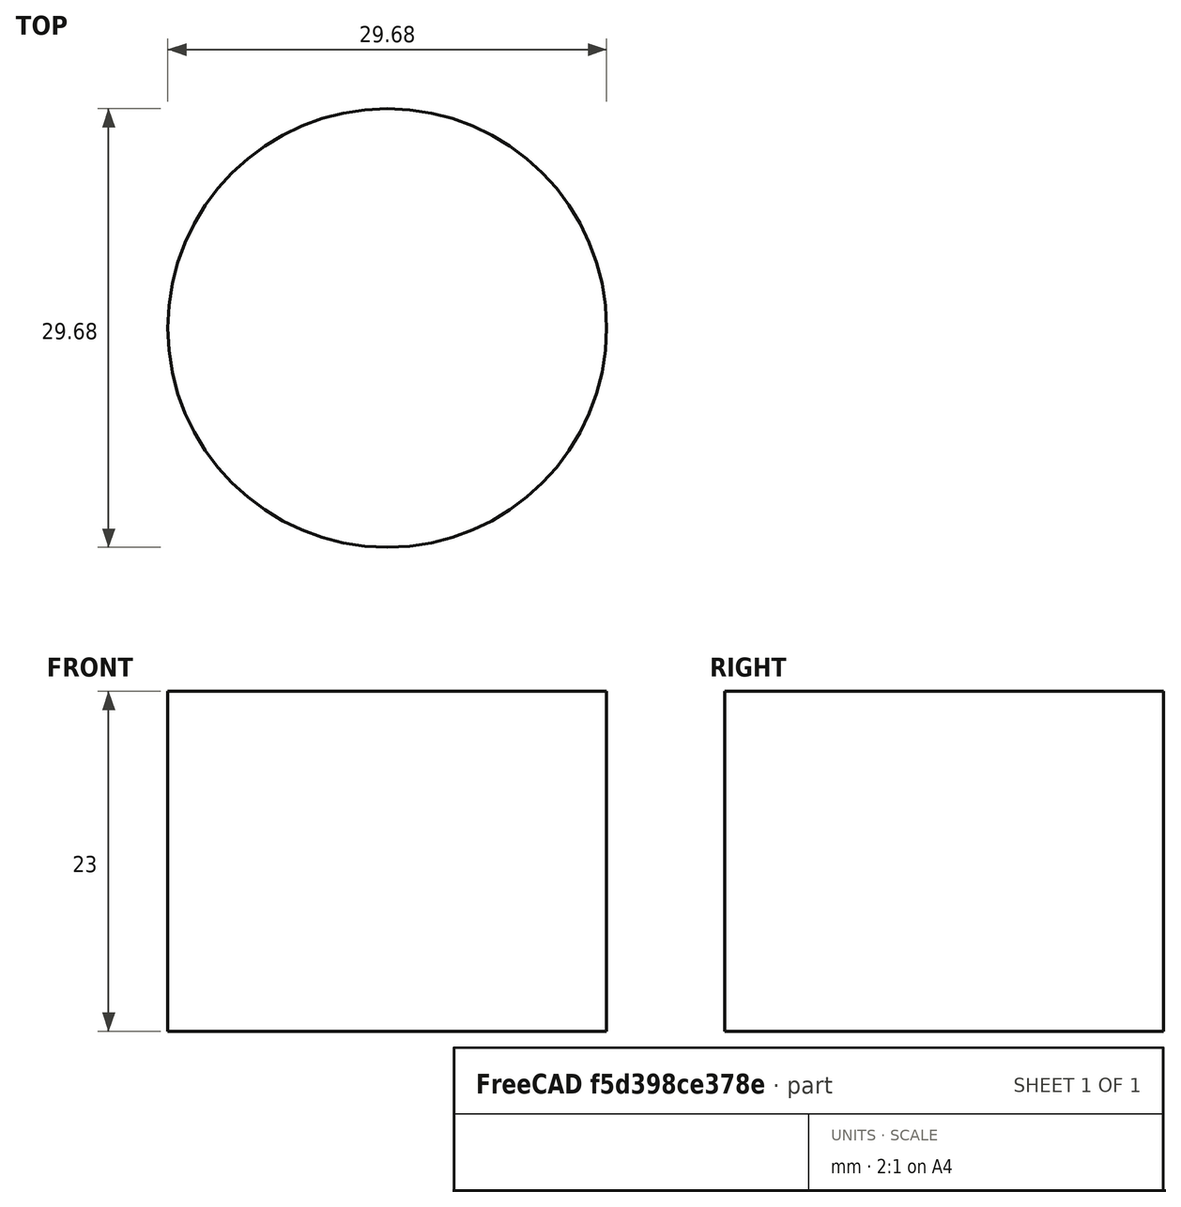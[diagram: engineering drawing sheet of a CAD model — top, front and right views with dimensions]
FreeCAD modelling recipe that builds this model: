
FCSTD DOCUMENT  (FreeCAD 0.17R13519 (Git))
Label: SFP-Puller2
License: All rights reserved
LicenseURL: http://en.wikipedia.org/wiki/All_rights_reserved
objects: TechDraw::DrawViewDimension×18, Sketcher::SketchObject×3, PartDesign::Pad×3, PartDesign::Fillet×3, Drawing::FeatureViewPart×3, TechDraw::DrawViewPart×3, Path::FeaturePython×3, Part::FeaturePython×2, PartDesign::Point×1, PartDesign::Line×1, PartDesign::SubtractiveCylinder×1, PartDesign::Pocket×1, PartDesign::Body×1, Drawing::FeaturePage×1, TechDraw::DrawSVGTemplate×1, TechDraw::DrawViewAnnotation×1, TechDraw::DrawPage×1, App::FeaturePython×1, Path::FeatureCompoundPython×1
note: 22 computed .brp shape members not serialized (recipe doc carries the construction recipe); baked Part::Feature solids carry a one-line shape summary decoded from their .brp

FEATURE [Sketcher::SketchObject] Sketch
  MapMode = 5
  Support = -> [XY_Plane]
  sketch-geometry (18):
    g0: LineSegment StartX=-1 StartY=5.95091 StartZ=0 EndX=-1 EndY=-5.54909 EndZ=0
    g1: LineSegment StartX=-1 StartY=-5.54909 StartZ=0 EndX=-8 EndY=-5.54909 EndZ=0
    g2: LineSegment StartX=-8 StartY=-5.54909 StartZ=0 EndX=-8 EndY=-9.54909 EndZ=0
    g3: LineSegment StartX=-8 StartY=-9.54909 StartZ=0 EndX=-4.78208 EndY=-12.304 EndZ=0
    g4: LineSegment StartX=-4.78208 StartY=-12.304 StartZ=0 EndX=-6.93768 EndY=-14.8219 EndZ=0
    g5: LineSegment StartX=-6.93768 StartY=-14.8219 StartZ=0 EndX=-2 EndY=-19.0491 EndZ=0
    g6: LineSegment StartX=-2 StartY=-19.0491 StartZ=0 EndX=0 EndY=-19.0491 EndZ=0
    g7: LineSegment StartX=-1 StartY=5.95091 StartZ=0 EndX=0 EndY=5.95091 EndZ=0
    g8: GeomPoint X=0 Y=-19.0491 Z=0
    g9: LineSegment StartX=0 StartY=-19.0491 StartZ=0 EndX=1 EndY=-19.0491 EndZ=0
    g10: LineSegment StartX=1 StartY=-19.0491 StartZ=0 EndX=1 EndY=-7.54909 EndZ=0
    g11: LineSegment StartX=1 StartY=-7.54909 StartZ=0 EndX=8 EndY=-7.54909 EndZ=0
    g12: LineSegment StartX=8 StartY=-7.54909 StartZ=0 EndX=8 EndY=-3.54909 EndZ=0
    g13: LineSegment StartX=8 StartY=-3.54909 StartZ=0 EndX=4.81331 EndY=-0.531755 EndZ=0
    g14: LineSegment StartX=4.81331 StartY=-0.531755 StartZ=0 EndX=6.7199 EndY=1.48185 EndZ=0
    g15: LineSegment StartX=6.7199 StartY=1.48185 StartZ=0 EndX=2 EndY=5.95091 EndZ=0
    g16: LineSegment StartX=0 StartY=5.95091 StartZ=0 EndX=2 EndY=5.95091 EndZ=0
    g17: GeomPoint X=0 Y=-6.54909 Z=0
  constraints (47):
    c: Vertical(g0)
    c: Coincident(g0,g1)
    c: Coincident(g1,g2)
    c: Vertical(g2)
    c: Coincident(g2,g3)
    c: Coincident(g3,g4)
    c: Coincident(g4,g5)
    c: Coincident(g6,g5)
    c: Horizontal(g6)
    c: Perpendicular(g1,g0)
    c: Perpendicular(g3,g4)
    c: Perpendicular(g4,g5)
    c: Coincident(g7,g0)
    c: PointOnObject(g7,g-2)
    c: Horizontal(g7)
    c: DistanceX(g7,g7) = 1
    c: DistanceX(g1,g1) = 7
    c: DistanceX(g6,g6) = 2
    c: PointOnObject(g8,g-2)
    c: Coincident(g8,g6)
    c: DistanceY(g2,g2) = 4
    c: Horizontal(g9)
    c: DistanceX(g9,g9) = 1
    c: Coincident(g9,g6)
    c: Vertical(g10)
    c: Coincident(g10,g9)
    c: Coincident(g11,g10)
    c: DistanceX(g11,g11) = 7
    c: Vertical(g12)
    c: DistanceY(g12,g12) = -4
    c: Coincident(g12,g11)
    c: Perpendicular(g11,g10)
    c: Coincident(g13,g12)
    c: Coincident(g14,g13)
    c: Perpendicular(g13,g14)
    c: Coincident(g15,g14)
    c: Perpendicular(g14,g15)
    c: Horizontal(g16)
    c: DistanceX(g16,g16) = 2
    c: Coincident(g16,g7)
    c: Coincident(g15,g16)
    c: DistanceY(g6,g7) = 25
    c: DistanceY(g10,g10) = 11.5
    c: DistanceY(g0,g0) = 11.5
    c: Symmetric(g0,g10,g17)  'RootPoint'
    c: Distance(g5) = 6.5
    c: Distance(g15) = 6.5
FEATURE [PartDesign::Pad] Pad
  Length = 3
  Length2 = 100
  Profile = -> Sketch
  Type = 0
FEATURE [PartDesign::Point] DatumPoint
  AttacherType = Attacher::AttachEnginePoint
  MapMode = 37
  Placement = pos=(-0.0215319,-6.59893,0) rot=(0,0,1;0rad)
  Support = -> [Pad]
FEATURE [PartDesign::Line] DatumLine
  AttacherType = Attacher::AttachEngineLine
  MapMode = 42
  Placement = pos=(-0.0215319,-6.59893,0) rot=(0,0,1;0rad)
  Support = -> [Pad]
FEATURE [Sketcher::SketchObject] Sketch001
  AttachmentOffset = pos=(0.26,-7.14,3) rot=(0,0,1;0rad)
  MapMode = 5
  Placement = pos=(0.26,-7.14,3) rot=(0,0,1;0rad)
  Support = -> [XY_Plane]
  sketch-geometry (1):
    g0: Circle CenterX=0 CenterY=0 CenterZ=0 NormalX=0 NormalY=0 NormalZ=1 AngleXU=0 Radius=5
  constraints (2):
    c: Radius(g0) = 5
    c: Coincident(g0,g-1)
FEATURE [PartDesign::Pad] Pad001
  BaseFeature = -> Pad
  Length = 20
  Length2 = 100
  Profile = -> Sketch001
  Type = 0
FEATURE [PartDesign::SubtractiveCylinder] Cylinder
  Angle = 360
  AttacherType = Attacher::AttachEngine3D
  AttachmentOffset = pos=(0.26,-7.14,0) rot=(0,0,1;0rad)
  BaseFeature = -> Pad001
  Height = 10
  MapMode = 5
  Placement = pos=(0.26,-7.14,23) rot=(0,0,1;0rad)
  Radius = 2.5
  Support = -> [Pad001]
FEATURE [PartDesign::Pocket] Pocket
  BaseFeature = -> Cylinder
  Length = 20
  Length2 = 100
  Placement = pos=(0.26,-7.14,23) rot=(0,0,1;0rad)
  Profile = -> Cylinder [Face24]
  Type = 0
FEATURE [Sketcher::SketchObject] Sketch002
  MapMode = 2
  Support = -> [Sketch]
  sketch-geometry (2):
    g0: GeomPoint X=0.26 Y=-7.14 Z=0
    g1: Circle CenterX=0.26 CenterY=-7.14 CenterZ=0 NormalX=0 NormalY=0 NormalZ=1 AngleXU=0 Radius=5
  constraints (4):
    c: DistanceX(g0) = 0.26
    c: DistanceY(g0) = -7.14
    c: Coincident(g1,g0)
    c: Radius(g1) = 5
FEATURE [PartDesign::Pad] Pad002
  BaseFeature = -> Pocket
  Length = 3
  Length2 = 100
  Placement = pos=(0.26,-7.14,23) rot=(0,0,1;0rad)
  Profile = -> Sketch002
  Type = 0
FEATURE [PartDesign::Fillet] Fillet
  Base = -> Pad002 [Edge8,Edge1,Edge63,Edge65,Edge31,Edge43]
  BaseFeature = -> Pad002
  Placement = pos=(0.26,-7.14,23) rot=(0,0,1;0rad)
  Radius = 0.95
FEATURE [PartDesign::Fillet] Fillet001
  Base = -> Fillet [Edge21,Edge18,Edge68,Edge70,Edge26,Edge71]
  BaseFeature = -> Fillet
  Placement = pos=(0.26,-7.14,23) rot=(0,0,1;0rad)
  Radius = 0.5
FEATURE [PartDesign::Fillet] Fillet002
  Base = -> Fillet001 [Edge58,Edge69]
  BaseFeature = -> Fillet001
  Placement = pos=(0.26,-7.14,23) rot=(0,0,1;0rad)
  Radius = 1
FEATURE [PartDesign::Body] Body
  Group = -> [Sketch,Pad,DatumPoint,DatumLine,Sketch001,Pad001,Cylinder,Pocket,Sketch002,Pad002,Fillet,Fillet001,Fillet002]
  Origin = -> Origin
  Tip = -> Fillet002
FEATURE [Drawing::FeatureViewPart] View
  Direction = (0,0,1)
  HiddenWidth = 0.15
  LineWidth = 0.35
  Rotation = 0
  Scale = 4
  ShowHiddenLines = true
  ShowSmoothLines = true
  Source = -> Body
  Tolerance = 0.05
  ViewResult = <blob: 11207 chars omitted>
  Visible = true
  X = 55
  Y = 45
FEATURE [Drawing::FeatureViewPart] View001
  Direction = (0,1,0)
  HiddenWidth = 0.15
  LineWidth = 0.35
  Rotation = 0
  Scale = 4
  ShowHiddenLines = true
  ShowSmoothLines = false
  Source = -> Body
  Tolerance = 0.05
  ViewResult = <blob: 10966 chars omitted>
  Visible = true
  X = 150
  Y = 55
FEATURE [Drawing::FeatureViewPart] View002
  Direction = (1,1,1)
  HiddenWidth = 0.15
  LineWidth = 0.35
  Rotation = 0
  Scale = 4
  ShowHiddenLines = true
  ShowSmoothLines = true
  Source = -> Body
  Tolerance = 0.05
  ViewResult = <blob: 16132 chars omitted>
  Visible = true
  X = 100
  Y = 110
FEATURE [Drawing::FeaturePage] Page
  EditableTexts = J Miller | 10-JUL-2018 | 4:1 | NA | SFP Pusher Adapter | Aluminium or engineering plastic | FCAD1 | 1
  Group = -> [View,View001,View002]
  Template = /Applications/FreeCAD.app/Contents/data/Mod/Drawing/Templates/A4_Landscape.svg
FEATURE [TechDraw::DrawSVGTemplate] Template
  EditableTexts = Designed_by_Name=J Miller; Drawing_number=FCAD-002; FC-Date=7-JUL-2018; FC-SC=4:1; FC-SH=1; FC-Title=Medrad-Puller; Subtitle=Aluminium or hard engineering plastic; Weight=NA
  Height = 210
  Orientation = 1
  Width = 297
FEATURE [TechDraw::DrawViewPart] View003  label="Top"
  CoarseView = true
  Direction = (0,0,1)
  Focus = 100
  HardHidden = true
  IsoCount = 0
  IsoHidden = true
  IsoVisible = true
  LockPosition = false
  Perspective = false
  Rotation = 0
  Scale = 4
  ScaleType = 0
  SeamHidden = true
  SeamVisible = true
  SmoothHidden = true
  SmoothVisible = true
  Source = -> [Body]
  X = 141.747
  Y = 133.6
FEATURE [TechDraw::DrawViewPart] View004  label="Side"
  CoarseView = true
  Direction = (1,0,0)
  Focus = 100
  HardHidden = true
  IsoCount = 0
  IsoHidden = false
  IsoVisible = true
  LockPosition = false
  Perspective = false
  Rotation = 0
  Scale = 4
  ScaleType = 0
  SeamHidden = true
  SeamVisible = true
  SmoothHidden = true
  SmoothVisible = true
  Source = -> [Body]
  X = 229.007
  Y = 104.62
FEATURE [TechDraw::DrawViewPart] View005  label="Third Angle"
  CoarseView = true
  Direction = (1,0,1)
  Focus = 100
  HardHidden = true
  IsoCount = 0
  IsoHidden = true
  IsoVisible = true
  LockPosition = false
  Perspective = false
  Rotation = 0
  Scale = 4
  ScaleType = 0
  SeamHidden = true
  SeamVisible = true
  SmoothHidden = true
  SmoothVisible = true
  Source = -> [Body]
  X = 60
  Y = 60
FEATURE [TechDraw::DrawViewDimension] Dimension
  FormatSpec = %.2f
  LockPosition = false
  MeasureType = 1
  References2D = -> [View004]
  Rotation = 0
  ScaleType = 0
  Type = 2
  X = -50
  Y = 0
FEATURE [TechDraw::DrawViewDimension] Dimension001
  FormatSpec = %.2f
  LockPosition = false
  MeasureType = 1
  References2D = -> [View004]
  Rotation = 0
  ScaleType = 0
  Type = 2
  X = -27.2112
  Y = 1.54609
FEATURE [TechDraw::DrawViewAnnotation] Annotation
  Font = osifont
  LineSpace = 80
  LockPosition = false
  MaxWidth = -1
  Rotation = 0
  ScaleType = 0
  Text = OD ø10 mm | ID M6 Tap (ø5 mm)
  TextSize = 8
  TextStyle = 0
  X = 46.3549
  Y = 180.581
FEATURE [TechDraw::DrawViewDimension] Dimension002
  FormatSpec = %.2f
  LockPosition = false
  MeasureType = 1
  References2D = -> [View003]
  Rotation = 0
  ScaleType = 0
  Type = 1
  X = 12.2377
  Y = -57.8095
FEATURE [TechDraw::DrawViewDimension] Dimension003
  FormatSpec = %.2f
  LockPosition = false
  MeasureType = 1
  References2D = -> [View003]
  Rotation = 0
  ScaleType = 0
  Type = 2
  X = -60.7966
  Y = 1.4057
FEATURE [TechDraw::DrawViewDimension] Dimension004
  FormatSpec = %.2f
  LockPosition = false
  MeasureType = 1
  References2D = -> [View003]
  Rotation = 0
  ScaleType = 0
  Type = 2
  X = -53.9438
  Y = -5.4471
FEATURE [TechDraw::DrawViewDimension] Dimension005
  FormatSpec = %.2f
  LockPosition = false
  MeasureType = 1
  References2D = -> [View003]
  Rotation = 0
  ScaleType = 0
  Type = 2
  X = -49.0239
  Y = -12.1242
FEATURE [TechDraw::DrawViewDimension] Dimension006
  FormatSpec = %.2f
  LockPosition = false
  MeasureType = 1
  References2D = -> [View003]
  Rotation = 0
  ScaleType = 0
  Type = 2
  X = -41.1168
  Y = -14.057
FEATURE [TechDraw::DrawViewDimension] Dimension007
  FormatSpec = %.2f
  LockPosition = false
  MeasureType = 1
  References2D = -> [View003]
  Rotation = 0
  ScaleType = 0
  Type = 0
  X = 11.8617
  Y = 46.1075
FEATURE [TechDraw::DrawViewDimension] Dimension008
  FormatSpec = %.2f
  LockPosition = false
  MeasureType = 1
  References2D = -> [View003]
  Rotation = 0
  ScaleType = 0
  Type = 0
  X = 34.0545
  Y = 28.6976
FEATURE [TechDraw::DrawViewDimension] Dimension009
  FormatSpec = %.2f
  LockPosition = false
  MeasureType = 1
  References2D = -> [View003]
  Rotation = 0
  ScaleType = 0
  Type = 0
  X = -16.4533
  Y = -24.68
FEATURE [TechDraw::DrawViewDimension] Dimension010
  FormatSpec = %.2f
  LockPosition = false
  MeasureType = 1
  References2D = -> [View003]
  Rotation = 0
  ScaleType = 0
  Type = 2
  X = -40.3342
  Y = 17.8052
FEATURE [TechDraw::DrawViewDimension] Dimension011
  FormatSpec = %.2f
  LockPosition = false
  MeasureType = 1
  References2D = -> [View003]
  Rotation = 0
  ScaleType = 0
  Type = 2
  X = -24.1642
  Y = 51.962
FEATURE [TechDraw::DrawViewDimension] Dimension012
  FormatSpec = %.2f
  LockPosition = false
  MeasureType = 1
  References2D = -> [View003]
  Rotation = 0
  ScaleType = 0
  Type = 2
  X = -15.8066
  Y = 40.8792
FEATURE [TechDraw::DrawViewDimension] Dimension013
  FormatSpec = %.2f
  LockPosition = false
  MeasureType = 1
  References2D = -> [View004]
  Rotation = 0
  ScaleType = 0
  Type = 2
  X = 43.1988
  Y = -3.7388
FEATURE [TechDraw::DrawViewDimension] Dimension014
  FormatSpec = %.2f
  LockPosition = false
  MeasureType = 1
  References2D = -> [View003]
  Rotation = 0
  ScaleType = 0
  Type = 6
  X = 8.33551
  Y = 35.5784
FEATURE [TechDraw::DrawViewDimension] Dimension015
  FormatSpec = %.2f
  LockPosition = false
  MeasureType = 1
  References2D = -> [View003]
  Rotation = 0
  ScaleType = 0
  Type = 6
  X = 21.957
  Y = 13.8248
FEATURE [TechDraw::DrawViewDimension] Dimension016
  FormatSpec = %.2f
  LockPosition = false
  MeasureType = 1
  References2D = -> [View003]
  Rotation = 0
  ScaleType = 0
  Type = 1
  X = 24.3966
  Y = -13.8248
FEATURE [TechDraw::DrawViewDimension] Dimension017
  FormatSpec = %.2f
  LockPosition = false
  MeasureType = 1
  References2D = -> [View003]
  Rotation = 0
  ScaleType = 0
  Type = 1
  X = -23.5834
  Y = 33.952
FEATURE [TechDraw::DrawPage] Page001
  KeepUpdated = true
  ProjectionType = 0
  Template = -> Template
  Views = -> [View003,View004,View005,Dimension,Dimension001,Annotation,Dimension002,Dimension003,Dimension004,Dimension005,Dimension006,Dimension007,Dimension008,Dimension009,Dimension010,Dimension011,Dimension012,Dimension013,Dimension014,Dimension015,Dimension016,Dimension017]
FEATURE [App::FeaturePython] SetupSheet  # Path/CAM operation (typed FeaturePython)
  ClearanceHeightExpression = StartDepth+SetupSheet.ClearanceHeightOffset
  ClearanceHeightOffset = 5
  FinalDepthExpression = OpFinalDepth
  HorizRapid = 0
  SafeHeightExpression = StartDepth+SetupSheet.SafeHeightOffset
  SafeHeightOffset = 3
  StartDepthExpression = OpStartDepth
  StepDownExpression = OpToolDiameter
  VertRapid = 0
FEATURE [Part::FeaturePython] Clone  label="Base-Body"  # Draft clone (typed FeaturePython)
  AttacherType = Attacher::AttachEngine3D
  Fuse = false
  Objects = -> [Body]
  PathResource = Base
  Scale = (1,1,1)
FEATURE [Part::FeaturePython] Stock001  # WARN: FeaturePython — macro-defined, semantics opaque (R4)
  Height = 23
  Placement = pos=(0,-6.54909,0) rot=(0,0,1;0rad)
  Radius = 14.84
  StockType = CreateCylinder
FEATURE [Path::FeaturePython] T2__2_5mm_cutter  label="T2: 2.5mm cutter"  # Path/CAM operation (typed FeaturePython)
  HorizFeed = 1.25
  HorizRapid = 0
  SpindleDir = 0
  SpindleSpeed = 3000
  ToolNumber = 2
  VertFeed = 1.25
  VertRapid = 0
  expr: HorizRapid = SetupSheet.HorizRapid
  expr: VertRapid = SetupSheet.VertRapid
FEATURE [Path::FeaturePython] Profile_Faces  # Path/CAM operation (typed FeaturePython)
  Active = true
  AreaParams:
    OpenMode = 0
    Angle = 45.0
    MinArcPoints = 4
    Coplanar = 0
    Tolerance = 1e-07
    CleanDistance = 0.0
    PocketExtraOffset = 0.0
    RoundPrecision = 0.0
    AngleShift = 0.0
    SubjectFill = 0
    PocketMode = 0
    Simplify = False
    SectionTolerance = 1e-06
    MaxArcPoints = 100
    Offset = 1.25
    Accuracy = 0.01
    PocketStepover = 0.0
    ClipFill = 0
    ToolRadius = 1.0
    Outline = False
    ClipperScale = 10000000.0
    FromCenter = False
    Explode = False
    EndType = 0
    Shift = 0.0
    ExtraPass = 0
    Project = False
    JoinType = 0
    Thicken = False
    Stepdown = 1.0
    SectionMode = 2
    MiterLimit = 2.0
    Deflection = 0.01
    Reorient = True
    FitArcs = True
    SectionCount = -1
    SectionOffset = 0.0
    Stepover = 0.0
    Unit = 1.0
    Fill = 0
  Base = -> [Clone]
  ClearanceHeight = 28
  Direction = 0
  FinalDepth = 1
  JoinType = 0
  MiterLimit = 0.1
  OffsetExtra = 0
  OpFinalDepth = 1
  OpStartDepth = 23
  OpToolDiameter = 2.5
  PathParams = {'resume_height': 26.0, 'feedrate': 1.25, 'verbose': True, 'orientation': 1, 'return_end': True, 'preamble': False, 'retraction': 28.0, 'feedrate_v': 1.25}
  SafeHeight = 26
  Side = 0
  StartDepth = 23
  StartPoint = (0,0,0)
  StepDown = 2.5
  ToolController = -> T2__2_5mm_cutter
  UseComp = true
  UseStartPoint = false
  processCircles = false
  processHoles = false
  processPerimeter = true
  expr: ClearanceHeight = StartDepth + SetupSheet.ClearanceHeightOffset
  expr: SafeHeight = StartDepth + SetupSheet.SafeHeightOffset
  expr: StepDown = OpToolDiameter
  expr: FinalDepth = OpFinalDepth
  expr: StartDepth = OpStartDepth
FEATURE [Path::FeatureCompoundPython] Operations  # Path/CAM operation (typed FeaturePython)
  Group = -> [Profile_Faces]
  UsePlacements = false
FEATURE [Path::FeaturePython] Job  # Path/CAM operation (typed FeaturePython)
  Base = -> Clone
  GeometryTolerance = 0.01
  Operations = -> Operations
  PostProcessor = 1
  SetupSheet = -> SetupSheet
  Stock = -> Stock001
  ToolController = -> [T2__2_5mm_cutter]
